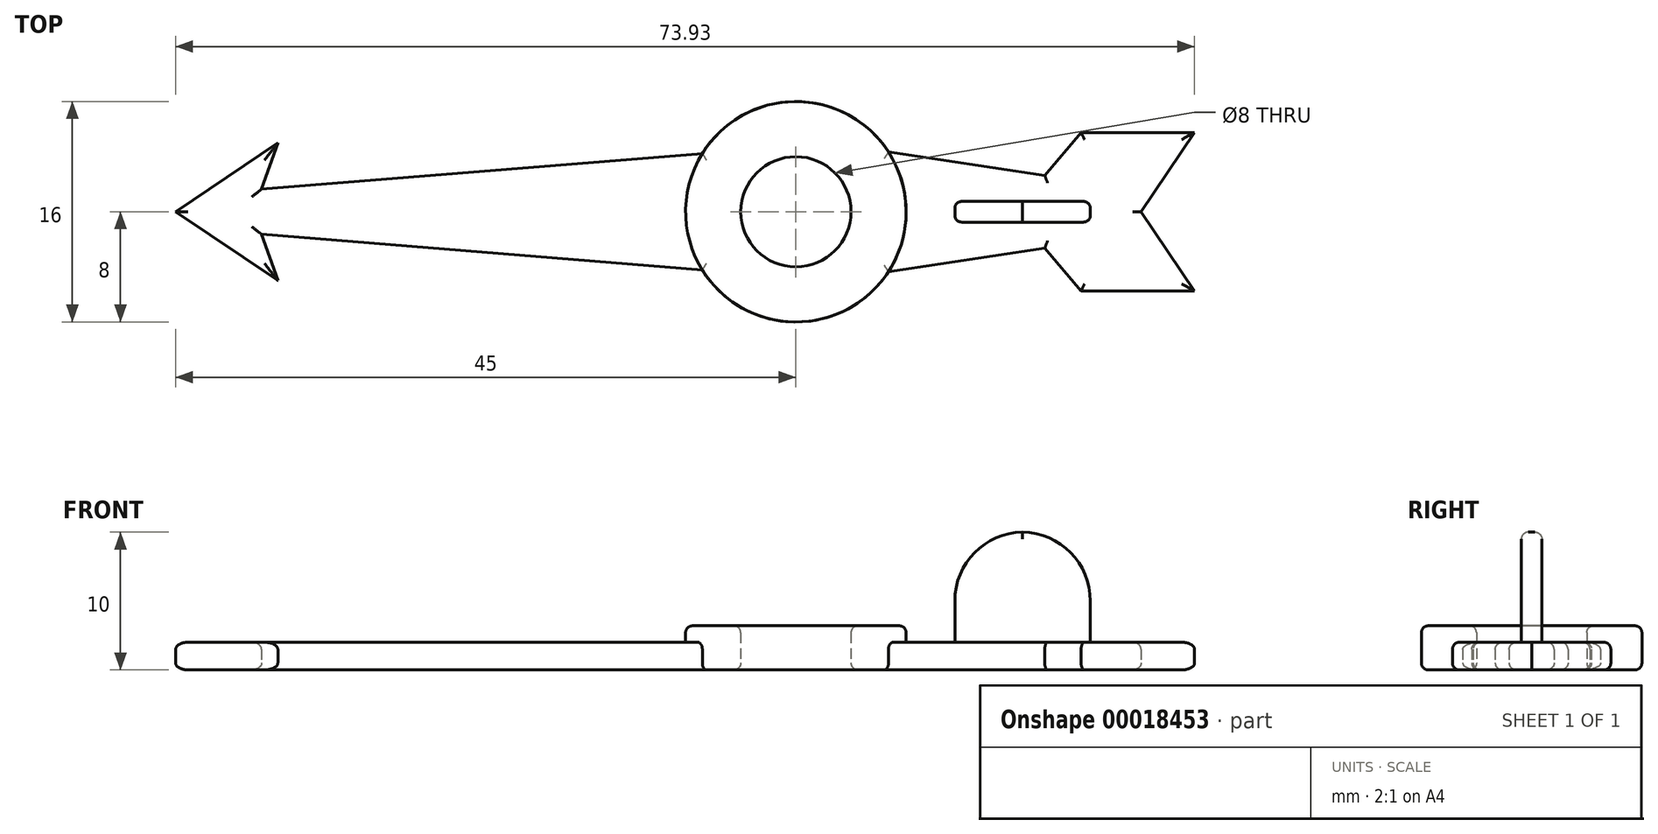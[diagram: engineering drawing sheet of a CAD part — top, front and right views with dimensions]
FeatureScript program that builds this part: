
annotation { "Feature Type Name" : "Feature", "Feature Type Description" : "" }
export const myFeature = defineFeature(function(context is Context, id is Id, definition is map)
    precondition{}
    {
        {
            var Q0;
            Q0=qCreatedBy(makeId("Top.planeOp"),FACE);
            var sketch = newSketch(context, id + "F0", { "sketchPlane" : qUnion([Q0])});
            skCircle(sketch, "E0", {"center": v(0, 0) * mm, "radius": 8 * mm});
            skCircle(sketch, "E1", {"center": v(0, 0) * mm, "radius": 4 * mm});
            skLineSegment(sketch, "E2", {"start": v(0, 0) * mm, "end": v(-45, 0) * mm, "construction": true});
            skLineSegment(sketch, "E3", {"start": v(-45, 0) * mm, "end": v(-37.58, 5) * mm});
            skLineSegment(sketch, "E4", {"start": v(-37.58, 5) * mm, "end": v(-38.76, 1.63) * mm});
            skLineSegment(sketch, "E5", {"start": v(-38.76, 1.63) * mm, "end": v(-6.79, 4.23) * mm});
            skLineSegment(sketch, "E6.0.MirrorCS", {"start": v(-45, 0) * mm, "end": v(-37.58, -5) * mm});
            skLineSegment(sketch, "E7.0.MirrorCS", {"start": v(-37.58, -5) * mm, "end": v(-38.76, -1.63) * mm});
            skLineSegment(sketch, "E8.0.MirrorCS", {"start": v(-38.76, -1.63) * mm, "end": v(-6.79, -4.23) * mm});
            skLineSegment(sketch, "E9", {"start": v(6.72, 4.34) * mm, "end": v(18.06, 2.64) * mm});
            skLineSegment(sketch, "E10", {"start": v(18.06, 2.64) * mm, "end": v(20.7, 5.75) * mm});
            skLineSegment(sketch, "E11", {"start": v(20.7, 5.75) * mm, "end": v(28.93, 5.75) * mm});
            skLineSegment(sketch, "E12", {"start": v(28.93, 5.75) * mm, "end": v(25.05, 0) * mm});
            skLineSegment(sketch, "E13.0.MirrorCS", {"start": v(6.72, -4.34) * mm, "end": v(18.06, -2.64) * mm});
            skLineSegment(sketch, "E14.0.MirrorCS", {"start": v(18.06, -2.64) * mm, "end": v(20.7, -5.75) * mm});
            skLineSegment(sketch, "E15.0.MirrorCS", {"start": v(20.7, -5.75) * mm, "end": v(28.93, -5.75) * mm});
            skLineSegment(sketch, "E16.0.MirrorCS", {"start": v(28.93, -5.75) * mm, "end": v(25.05, 0) * mm});
            skSolve(sketch);
        }
        {
            var Q0;
            Q0=makeQuery(id+"F0.imprint","IMPRINT",FACE,{"disambiguationData":[TD([[makeQuery(id+"F0.imprint","IMPRINT",EDGE,{"derivedFrom":sQuery(id+"F0.wireOp",EDGE,"E1")}),-1.0]])]});
            extrude(context, id + "F1", {"entities" : qUnion([Q0]), "depth" : 3.2 * mm});
        }
        {
            var Q0;
            {var subQ1=sQuery(id+"F0.wireOp",EDGE,"E9");Q0=makeQuery(id+"F0.imprint","IMPRINT",FACE,{"disambiguationData":[TD([[makeQuery(id+"F0.imprint","IMPRINT",EDGE,{"derivedFrom":subQ1}),-1.0]])]});}
            var Q1;
            Q1=makeQuery(id+"F0.imprint","IMPRINT",FACE,{"disambiguationData":[TD([[makeQuery(id+"F0.imprint","IMPRINT",EDGE,{"derivedFrom":sQuery(id+"F0.wireOp",EDGE,"E3")}),-1.0]])]});
            extrude(context, id + "F2", {"entities" : qUnion([Q0, Q1]), "operationType" : NewBodyOperationType.ADD, "depth" : 2 * mm});
        }
        {
            var Q0;
            Q0=makeQuery(id+"F1.opExtrude","CAP_EDGE",EDGE,{"disambiguationData":[OSD([sQuery(id+"F0.wireOp",EDGE,"E0")])],"isStart":false});
            var Q1;
            Q1=makeQuery(id+"F1.opExtrude","CAP_EDGE",EDGE,{"disambiguationData":[OSD([sQuery(id+"F0.wireOp",EDGE,"E1")])],"isStart":false});
            var Q2;
            Q2=makeQuery(id+"F2.opExtrude","CAP_EDGE",EDGE,{"disambiguationData":[OSD([sQuery(id+"F0.wireOp",EDGE,"E13.0.MirrorCS")])],"isStart":false});
            var Q3;
            Q3=makeQuery(id+"F2.opExtrude","CAP_EDGE",EDGE,{"disambiguationData":[OSD([sQuery(id+"F0.wireOp",EDGE,"E14.0.MirrorCS")])],"isStart":false});
            var Q4;
            Q4=makeQuery(id+"F2.opExtrude","CAP_EDGE",EDGE,{"disambiguationData":[OSD([sQuery(id+"F0.wireOp",EDGE,"E15.0.MirrorCS")])],"isStart":false});
            var Q5;
            Q5=makeQuery(id+"F2.opExtrude","CAP_EDGE",EDGE,{"disambiguationData":[OSD([sQuery(id+"F0.wireOp",EDGE,"E16.0.MirrorCS")])],"isStart":false});
            var Q6;
            Q6=makeQuery(id+"F2.opExtrude","CAP_EDGE",EDGE,{"disambiguationData":[OSD([sQuery(id+"F0.wireOp",EDGE,"E12")])],"isStart":false});
            var Q7;
            Q7=makeQuery(id+"F2.opExtrude","CAP_EDGE",EDGE,{"disambiguationData":[OSD([sQuery(id+"F0.wireOp",EDGE,"E11")])],"isStart":false});
            var Q8;
            Q8=makeQuery(id+"F2.opExtrude","CAP_EDGE",EDGE,{"disambiguationData":[OSD([sQuery(id+"F0.wireOp",EDGE,"E10")])],"isStart":false});
            var Q9;
            Q9=makeQuery(id+"F2.opExtrude","CAP_EDGE",EDGE,{"disambiguationData":[OSD([sQuery(id+"F0.wireOp",EDGE,"E9")])],"isStart":false});
            var Q10;
            Q10=makeQuery(id+"F2.opExtrude","CAP_EDGE",EDGE,{"disambiguationData":[OSD([sQuery(id+"F0.wireOp",EDGE,"E8.0.MirrorCS")])],"isStart":false});
            var Q11;
            Q11=makeQuery(id+"F2.opExtrude","CAP_EDGE",EDGE,{"disambiguationData":[OSD([sQuery(id+"F0.wireOp",EDGE,"E7.0.MirrorCS")])],"isStart":false});
            var Q12;
            Q12=makeQuery(id+"F2.opExtrude","CAP_EDGE",EDGE,{"disambiguationData":[OSD([sQuery(id+"F0.wireOp",EDGE,"E6.0.MirrorCS")])],"isStart":false});
            var Q13;
            Q13=makeQuery(id+"F2.opExtrude","CAP_EDGE",EDGE,{"disambiguationData":[OSD([sQuery(id+"F0.wireOp",EDGE,"E3")])],"isStart":false});
            var Q14;
            Q14=makeQuery(id+"F2.opExtrude","CAP_EDGE",EDGE,{"disambiguationData":[OSD([sQuery(id+"F0.wireOp",EDGE,"E4")])],"isStart":false});
            var Q15;
            Q15=makeQuery(id+"F2.opExtrude","CAP_EDGE",EDGE,{"disambiguationData":[OSD([sQuery(id+"F0.wireOp",EDGE,"E5")])],"isStart":false});
            fillet(context, id + "F3", {"entities" : qUnion([Q0, Q1, Q2, Q3, Q4, Q5, Q6, Q7, Q8, Q9, Q10, Q11, Q12, Q13, Q14, Q15]), "radius" : 0.5 * mm, "allowEdgeOverflow" : false});
        }
        {
            var Q0;
            {var subQ0=sQuery(id+"F0.wireOp",EDGE,"E0");var subQ2=sQuery(id+"F0.wireOp",EDGE,"E8.0.MirrorCS");Q0=makeQuery(id+"F2.boolean.opBoolean","SPLIT",EDGE,{"disambiguationData":[TD([makeQuery(id+"F2.opExtrude","SWEPT_FACE",FACE,{"disambiguationData":[OSD([subQ2])]})])],"derivedFrom":makeQuery(id+"F1.opExtrude","CAP_EDGE",EDGE,{"disambiguationData":[OSD([subQ0])],"isStart":true})});}
            var Q1;
            {var subQ0=sQuery(id+"F0.wireOp",EDGE,"E0");var subQ2=sQuery(id+"F0.wireOp",EDGE,"E5");Q1=makeQuery(id+"F2.boolean.opBoolean","SPLIT",EDGE,{"disambiguationData":[TD([makeQuery(id+"F2.opExtrude","SWEPT_FACE",FACE,{"disambiguationData":[OSD([subQ2])]})])],"derivedFrom":makeQuery(id+"F1.opExtrude","CAP_EDGE",EDGE,{"disambiguationData":[OSD([subQ0])],"isStart":true})});}
            var Q2;
            Q2=makeQuery(id+"F2.opExtrude","CAP_EDGE",EDGE,{"disambiguationData":[OSD([sQuery(id+"F0.wireOp",EDGE,"E5")])],"isStart":true});
            var Q3;
            Q3=makeQuery(id+"F2.opExtrude","CAP_EDGE",EDGE,{"disambiguationData":[OSD([sQuery(id+"F0.wireOp",EDGE,"E4")])],"isStart":true});
            var Q4;
            Q4=makeQuery(id+"F2.opExtrude","CAP_EDGE",EDGE,{"disambiguationData":[OSD([sQuery(id+"F0.wireOp",EDGE,"E3")])],"isStart":true});
            var Q5;
            Q5=makeQuery(id+"F2.opExtrude","CAP_EDGE",EDGE,{"disambiguationData":[OSD([sQuery(id+"F0.wireOp",EDGE,"E6.0.MirrorCS")])],"isStart":true});
            var Q6;
            Q6=makeQuery(id+"F2.opExtrude","CAP_EDGE",EDGE,{"disambiguationData":[OSD([sQuery(id+"F0.wireOp",EDGE,"E7.0.MirrorCS")])],"isStart":true});
            var Q7;
            Q7=makeQuery(id+"F2.opExtrude","CAP_EDGE",EDGE,{"disambiguationData":[OSD([sQuery(id+"F0.wireOp",EDGE,"E8.0.MirrorCS")])],"isStart":true});
            var Q8;
            Q8=makeQuery(id+"F2.opExtrude","CAP_EDGE",EDGE,{"disambiguationData":[OSD([sQuery(id+"F0.wireOp",EDGE,"E13.0.MirrorCS")])],"isStart":true});
            var Q9;
            Q9=makeQuery(id+"F2.opExtrude","CAP_EDGE",EDGE,{"disambiguationData":[OSD([sQuery(id+"F0.wireOp",EDGE,"E14.0.MirrorCS")])],"isStart":true});
            var Q10;
            Q10=makeQuery(id+"F2.opExtrude","CAP_EDGE",EDGE,{"disambiguationData":[OSD([sQuery(id+"F0.wireOp",EDGE,"E15.0.MirrorCS")])],"isStart":true});
            var Q11;
            Q11=makeQuery(id+"F2.opExtrude","CAP_EDGE",EDGE,{"disambiguationData":[OSD([sQuery(id+"F0.wireOp",EDGE,"E16.0.MirrorCS")])],"isStart":true});
            var Q12;
            Q12=makeQuery(id+"F2.opExtrude","CAP_EDGE",EDGE,{"disambiguationData":[OSD([sQuery(id+"F0.wireOp",EDGE,"E12")])],"isStart":true});
            var Q13;
            Q13=makeQuery(id+"F2.opExtrude","CAP_EDGE",EDGE,{"disambiguationData":[OSD([sQuery(id+"F0.wireOp",EDGE,"E11")])],"isStart":true});
            var Q14;
            Q14=makeQuery(id+"F2.opExtrude","CAP_EDGE",EDGE,{"disambiguationData":[OSD([sQuery(id+"F0.wireOp",EDGE,"E10")])],"isStart":true});
            var Q15;
            Q15=makeQuery(id+"F2.opExtrude","CAP_EDGE",EDGE,{"disambiguationData":[OSD([sQuery(id+"F0.wireOp",EDGE,"E9")])],"isStart":true});
            var Q16;
            Q16=makeQuery(id+"F1.opExtrude","CAP_EDGE",EDGE,{"disambiguationData":[OSD([sQuery(id+"F0.wireOp",EDGE,"E1")])],"isStart":true});
            fillet(context, id + "F4", {"entities" : qUnion([Q0, Q1, Q2, Q3, Q4, Q5, Q6, Q7, Q8, Q9, Q10, Q11, Q12, Q13, Q14, Q15, Q16]), "radius" : 0.5 * mm, "allowEdgeOverflow" : false});
        }
        {
            var Q0;
            Q0=makeQuery(id+"F2.opExtrude","CAP_FACE",FACE,{"disambiguationData":[OSD([sQuery(id+"F0.wireOp",EDGE,"E0"),sQuery(id+"F0.wireOp",EDGE,"E9"),sQuery(id+"F0.wireOp",EDGE,"E10"),sQuery(id+"F0.wireOp",EDGE,"E11"),sQuery(id+"F0.wireOp",EDGE,"E12"),sQuery(id+"F0.wireOp",EDGE,"E13.0.MirrorCS"),sQuery(id+"F0.wireOp",EDGE,"E14.0.MirrorCS"),sQuery(id+"F0.wireOp",EDGE,"E15.0.MirrorCS"),sQuery(id+"F0.wireOp",EDGE,"E16.0.MirrorCS")])],"isStart":false});
            var sketch = newSketch(context, id + "F5", { "sketchPlane" : qUnion([Q0])});
            skLineSegment(sketch, "E17", {"start": v(0, 0) * mm, "end": v(24.44, 0) * mm, "construction": true});
            skLineSegment(sketch, "E18.rect.bottom", {"start": v(21.36, 0.75) * mm, "end": v(11.53, 0.75) * mm});
            skLineSegment(sketch, "E18.rect.top", {"start": v(21.36, -0.75) * mm, "end": v(11.53, -0.75) * mm});
            skLineSegment(sketch, "E18.rect.left", {"start": v(21.36, 0.75) * mm, "end": v(21.36, -0.75) * mm});
            skLineSegment(sketch, "E18.rect.right", {"start": v(11.53, 0.75) * mm, "end": v(11.53, -0.75) * mm});
            skPoint(sketch, "E18.rect.middle", {"position": v(16.45, 0) * mm});
            skSolve(sketch);
        }
        {
            var Q0;
            Q0=makeQuery(id+"F5.imprint","IMPRINT",FACE,{"disambiguationData":[TD([[makeQuery(id+"F5.imprint","IMPRINT",EDGE,{"derivedFrom":sQuery(id+"F5.wireOp",EDGE,"E18.rect.bottom")}),1.0]])]});
            extrude(context, id + "F6", {"entities" : qUnion([Q0]), "operationType" : NewBodyOperationType.ADD, "depth" : 8 * mm});
        }
        {
            var Q0;
            Q0=makeQuery(id+"F6.opExtrude","CAP_EDGE",EDGE,{"disambiguationData":[OSD([sQuery(id+"F5.wireOp",EDGE,"E18.rect.right")])],"isStart":false});
            var Q1;
            Q1=makeQuery(id+"F6.opExtrude","CAP_EDGE",EDGE,{"disambiguationData":[OSD([sQuery(id+"F5.wireOp",EDGE,"E18.rect.left")])],"isStart":false});
            fillet(context, id + "F7", {"entities" : qUnion([Q0, Q1]), "radius" : 5 * mm, "tangentPropagation" : true, "allowEdgeOverflow" : false});
        }
        {
            var Q0;
            Q0=makeQuery(id+"F7.opFillet","BLEND_EDGE",EDGE,{"blendedFrom":[makeQuery(id+"F6.opExtrude","CAP_EDGE",EDGE,{"disambiguationData":[OSD([sQuery(id+"F5.wireOp",EDGE,"E18.rect.right")])],"isStart":false}),makeQuery(id+"F6.opExtrude","SWEPT_FACE",FACE,{"disambiguationData":[OSD([sQuery(id+"F5.wireOp",EDGE,"E18.rect.top")])]})],"blendedInto":[makeQuery(id+"F6.opExtrude","SWEPT_FACE",FACE,{"disambiguationData":[OSD([sQuery(id+"F5.wireOp",EDGE,"E18.rect.top")])]})]});
            var Q1;
            Q1=makeQuery(id+"F7.opFillet","BLEND_EDGE",EDGE,{"blendedFrom":[makeQuery(id+"F6.opExtrude","CAP_EDGE",EDGE,{"disambiguationData":[OSD([sQuery(id+"F5.wireOp",EDGE,"E18.rect.left")])],"isStart":false}),makeQuery(id+"F6.opExtrude","SWEPT_FACE",FACE,{"disambiguationData":[OSD([sQuery(id+"F5.wireOp",EDGE,"E18.rect.top")])]})],"blendedInto":[makeQuery(id+"F6.opExtrude","SWEPT_FACE",FACE,{"disambiguationData":[OSD([sQuery(id+"F5.wireOp",EDGE,"E18.rect.top")])]})]});
            var Q2;
            Q2=makeQuery(id+"F7.opFillet","BLEND_EDGE",EDGE,{"blendedFrom":[makeQuery(id+"F6.opExtrude","CAP_EDGE",EDGE,{"disambiguationData":[OSD([sQuery(id+"F5.wireOp",EDGE,"E18.rect.left")])],"isStart":false}),makeQuery(id+"F6.opExtrude","SWEPT_FACE",FACE,{"disambiguationData":[OSD([sQuery(id+"F5.wireOp",EDGE,"E18.rect.bottom")])]})],"blendedInto":[makeQuery(id+"F6.opExtrude","SWEPT_FACE",FACE,{"disambiguationData":[OSD([sQuery(id+"F5.wireOp",EDGE,"E18.rect.bottom")])]})]});
            var Q3;
            Q3=makeQuery(id+"F7.opFillet","BLEND_EDGE",EDGE,{"blendedFrom":[makeQuery(id+"F6.opExtrude","CAP_EDGE",EDGE,{"disambiguationData":[OSD([sQuery(id+"F5.wireOp",EDGE,"E18.rect.right")])],"isStart":false}),makeQuery(id+"F6.opExtrude","SWEPT_FACE",FACE,{"disambiguationData":[OSD([sQuery(id+"F5.wireOp",EDGE,"E18.rect.bottom")])]})],"blendedInto":[makeQuery(id+"F6.opExtrude","SWEPT_FACE",FACE,{"disambiguationData":[OSD([sQuery(id+"F5.wireOp",EDGE,"E18.rect.bottom")])]})]});
            fillet(context, id + "F8", {"entities" : qUnion([Q0, Q1, Q2, Q3]), "radius" : .5 * mm, "tangentPropagation" : true, "allowEdgeOverflow" : false});
        }
    });
